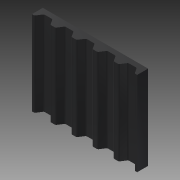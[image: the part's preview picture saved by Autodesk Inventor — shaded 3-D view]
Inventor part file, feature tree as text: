
AUTODESK INVENTOR PART (.ipt)
format: ipt  version: 2015 SP1 (Build 190203100, 203)  size: 165,888 bytes
history: native  units: mm
features: other x3, extrude x1, pattern_linear x1, sketch x1
ambient origin geometry x8: Origin, YZ Plane, XZ Plane, XY Plane, X Axis, Y Axis, Z Axis, Center Point
bodies: Solid1 (feature_tree)
feature tree (6):
  other  "Table"
  other  "T2.5 belt-01"
  other  "T2.5 belt-10"
  extrude  "Extrusion1"  Depth=0.2mm
  pattern_linear  "Rectangular Pattern1"  Spacing1=0.2mm  [1 undecoded]
  sketch  "Sketch1"  dims[d5=0.3mm d7=0.2mm d8=0.2mm d9=50.0mm d11=2.5mm d12=10.0mm d14=10.0mm d16=1.3mm d17=10.0mm d18=0.0mm d21=12.5mm]
note: 1 required parameter value undecoded (feature->parameter linkage not recoverable at this tier; creation-order binding heuristic only, values carry confidence <= 0.55)
